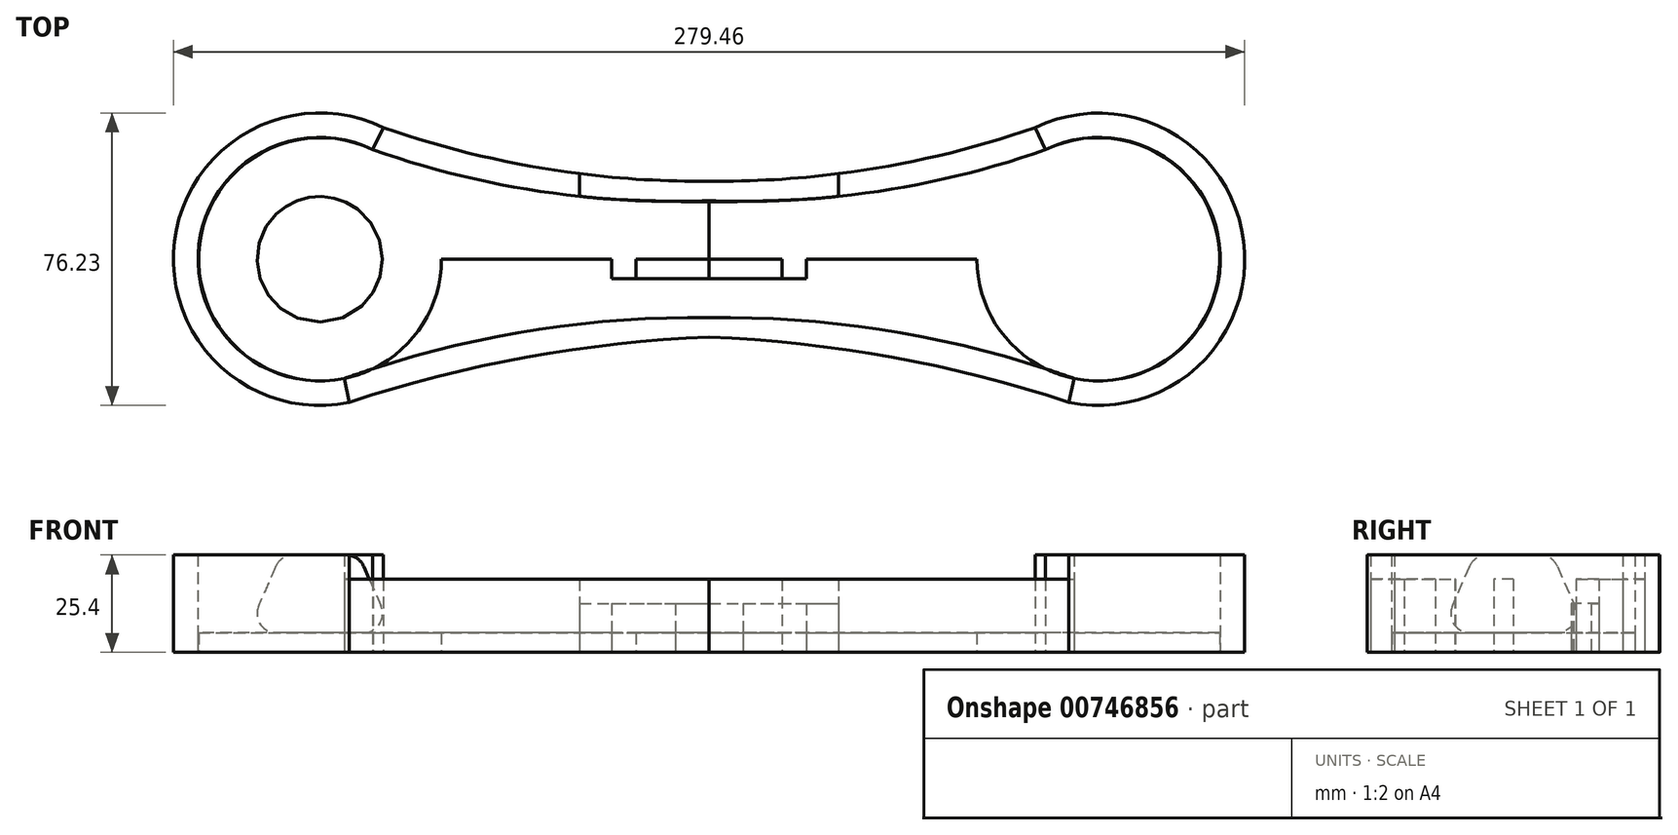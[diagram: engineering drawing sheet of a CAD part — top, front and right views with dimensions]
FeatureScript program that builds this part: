
annotation { "Feature Type Name" : "Feature", "Feature Type Description" : "" }
export const myFeature = defineFeature(function(context is Context, id is Id, definition is map)
    precondition{}
    {
        {
            var Q0;
            Q0=qCreatedBy(makeId("Top.planeOp"),FACE);
            var sketch = newSketch(context, id + "F0", { "sketchPlane" : qUnion([Q0])});
            skLineSegment(sketch, "E0", {"start": v(0, 0) * mm, "end": v(101.6, 0) * mm});
            skCircle(sketch, "E1", {"center": v(101.6, 0) * mm, "radius": 38.1 * mm});
            skCircle(sketch, "E2", {"center": v(101.6, 0) * mm, "radius": 31.75 * mm});
            skLineSegment(sketch, "E3", {"start": v(0, 0) * mm, "end": v(0, 20.32) * mm});
            skLineSegment(sketch, "E4", {"start": v(0, 0) * mm, "end": v(0, -20.32) * mm});
            skPoint(sketch, "E5.endSnap0", {"position": v(93.85, -17.4) * mm});
            skLineSegment(sketch, "E6", {"start": v(93.85, -37.3) * mm, "end": v(95.14, -31.09) * mm});
            skLineSegment(sketch, "E7", {"start": v(85, 34.3) * mm, "end": v(87.76, 28.58) * mm});
            skArc(sketch, "E8", {"start": v(95.14, -31.09) * mm, "mid": v(132.94, 3.88) * mm, "end": v(87.76, 28.58) * mm});
            skArc(sketch, "E9", {"start": v(93.85, -37.3) * mm, "mid": v(139.47, 4.68) * mm, "end": v(85, 34.3) * mm});
            skArc(sketch, "E10", {"start": v(93.85, -37.3) * mm, "mid": v(47.52, -25.54) * mm, "end": v(0, -20.32) * mm});
            skLineSegment(sketch, "E11.MirrorCS", {"start": v(-93.85, -37.3) * mm, "end": v(-95.14, -31.09) * mm});
            skLineSegment(sketch, "E12.MirrorCS", {"start": v(-85, 34.3) * mm, "end": v(-87.76, 28.58) * mm});
            skPoint(sketch, "E13.MirrorP", {"position": v(-93.85, -17.4) * mm});
            skArc(sketch, "E14.MirrorCS", {"start": v(-95.14, -31.09) * mm, "mid": v(-132.94, 3.88) * mm, "end": v(-87.76, 28.58) * mm});
            skCircle(sketch, "E15.MirrorC", {"center": v(-101.6, 0) * mm, "radius": 31.75 * mm});
            skLineSegment(sketch, "E16.MirrorCS", {"start": v(0, 0) * mm, "end": v(-101.6, 0) * mm});
            skArc(sketch, "E17.MirrorCS", {"start": v(-93.85, -37.3) * mm, "mid": v(-47.52, -25.54) * mm, "end": v(0, -20.32) * mm});
            skArc(sketch, "E18.MirrorCS", {"start": v(-93.85, -37.3) * mm, "mid": v(-139.47, 4.68) * mm, "end": v(-85, 34.3) * mm});
            skArc(sketch, "E19", {"start": v(0, 20.32) * mm, "mid": v(43.1, 23.67) * mm, "end": v(85, 34.3) * mm});
            skArc(sketch, "E20.MirrorCS", {"start": v(0, 20.32) * mm, "mid": v(-43.1, 23.67) * mm, "end": v(-85, 34.3) * mm});
            skLineSegment(sketch, "E21", {"start": v(0, 0) * mm, "end": v(-25.4, 0) * mm});
            skLineSegment(sketch, "E22", {"start": v(0, 0) * mm, "end": v(19.05, 0) * mm});
            skLineSegment(sketch, "E23", {"start": v(-25.4, 0) * mm, "end": v(-25.4, -5.08) * mm});
            skLineSegment(sketch, "E24", {"start": v(-25.4, -5.08) * mm, "end": v(19.05, -5.08) * mm});
            skLineSegment(sketch, "E25", {"start": v(19.05, -5.08) * mm, "end": v(19.05, 0) * mm});
            skArc(sketch, "E26", {"start": v(95.14, -31.09) * mm, "mid": v(48.28, -18.9) * mm, "end": v(0, -15.24) * mm});
            skArc(sketch, "E27.MirrorCS", {"start": v(-95.14, -31.09) * mm, "mid": v(-48.28, -18.9) * mm, "end": v(0, -15.24) * mm});
            skArc(sketch, "E28", {"start": v(0, 15.24) * mm, "mid": v(44.51, 17.76) * mm, "end": v(87.76, 28.58) * mm});
            skArc(sketch, "E29.MirrorCS", {"start": v(0, 15.24) * mm, "mid": v(-44.51, 17.76) * mm, "end": v(-87.76, 28.58) * mm});
            skLineSegment(sketch, "E30", {"start": v(19.05, 20.9) * mm, "end": v(-25.4, 21.4) * mm});
            skLineSegment(sketch, "E31", {"start": v(-25.4, 15.65) * mm, "end": v(-25.4, 21.4) * mm});
            skLineSegment(sketch, "E32", {"start": v(0, 0) * mm, "end": v(25.4, 0) * mm});
            skLineSegment(sketch, "E33", {"start": v(25.4, 0) * mm, "end": v(25.4, 21.4) * mm});
            skArc(sketch, "E34", {"start": v(-25.4, 15.65) * mm, "mid": v(0, 15) * mm, "end": v(25.4, 15.65) * mm});
            skLineSegment(sketch, "E35", {"start": v(-33.78, 22.32) * mm, "end": v(-33.78, 16.38) * mm});
            skLineSegment(sketch, "E36", {"start": v(33.78, 22.32) * mm, "end": v(33.78, 16.38) * mm});
            skSolve(sketch);
        }
        {
            var Q0;
            {var subQ1=sQuery(id+"F0.wireOp",EDGE,"E6");Q0=makeQuery(id+"F0.imprint","IMPRINT",FACE,{"disambiguationData":[TD([[makeQuery(id+"F0.imprint","IMPRINT",EDGE,{"derivedFrom":subQ1}),-1.0]])]});}
            var Q1;
            {var subQ0=sQuery(id+"F0.wireOp",EDGE,"E11.MirrorCS");Q1=makeQuery(id+"F0.imprint","IMPRINT",FACE,{"disambiguationData":[TD([[makeQuery(id+"F0.imprint","IMPRINT",EDGE,{"derivedFrom":subQ0}),1.0]])]});}
            extrude(context, id + "F1", {"entities" : qUnion([Q0, Q1]), "depth" : 25.4 * mm, "offsetDistance" : 25.4 * mm});
        }
        {
            var Q0;
            {var subQ0=sQuery(id+"F0.wireOp",EDGE,"E22");Q0=makeQuery(id+"F0.imprint","IMPRINT",FACE,{"disambiguationData":[TD([[makeQuery(id+"F0.imprint","IMPRINT",EDGE,{"derivedFrom":subQ0}),-1.0]])]});}
            var Q1;
            {var subQ0=sQuery(id+"F0.wireOp",EDGE,"E8");Q1=makeQuery(id+"F0.imprint","IMPRINT",FACE,{"disambiguationData":[TD([[makeQuery(id+"F0.imprint","IMPRINT",EDGE,{"derivedFrom":subQ0}),1.0]])]});}
            var Q2;
            {var subQ0=sQuery(id+"F0.wireOp",EDGE,"E14.MirrorCS");Q2=makeQuery(id+"F0.imprint","IMPRINT",FACE,{"disambiguationData":[TD([[makeQuery(id+"F0.imprint","IMPRINT",EDGE,{"derivedFrom":subQ0}),-1.0]])]});}
            var Q3;
            {var subQ0=sQuery(id+"F0.wireOp",EDGE,"E21");Q3=makeQuery(id+"F0.imprint","IMPRINT",FACE,{"disambiguationData":[TD([[makeQuery(id+"F0.imprint","IMPRINT",EDGE,{"derivedFrom":subQ0}),1.0]])]});}
            var Q4;
            {var subQ0=sQuery(id+"F0.wireOp",EDGE,"E25");Q4=makeQuery(id+"F0.imprint","IMPRINT",FACE,{"disambiguationData":[TD([[makeQuery(id+"F0.imprint","IMPRINT",EDGE,{"derivedFrom":subQ0}),-1.0]])]});}
            var Q5;
            {var subQ0=sQuery(id+"F0.wireOp",EDGE,"E23");Q5=makeQuery(id+"F0.imprint","IMPRINT",FACE,{"disambiguationData":[TD([[makeQuery(id+"F0.imprint","IMPRINT",EDGE,{"derivedFrom":subQ0}),-1.0]])]});}
            var Q6;
            {var subQ0=sQuery(id+"F0.wireOp",EDGE,"E21");Q6=makeQuery(id+"F0.imprint","IMPRINT",FACE,{"disambiguationData":[TD([[makeQuery(id+"F0.imprint","IMPRINT",EDGE,{"derivedFrom":subQ0}),-1.0]])]});}
            var Q7;
            {var subQ0=sQuery(id+"F0.wireOp",EDGE,"E22");Q7=makeQuery(id+"F0.imprint","IMPRINT",FACE,{"disambiguationData":[TD([[makeQuery(id+"F0.imprint","IMPRINT",EDGE,{"derivedFrom":subQ0}),1.0]])]});}
            var Q8;
            {var subQ0=sQuery(id+"F0.wireOp",EDGE,"E2");var subQ1=sQuery(id+"F0.wireOp",EDGE,"E0");var subQ2=makeQuery(id+"F0.imprint","INTERSECT",VERTEX,{"derivedFrom":[subQ1,subQ0]});Q8=makeQuery(id+"F0.imprint","IMPRINT",FACE,{"disambiguationData":[TD([[makeQuery(id+"F0.imprint","IMPRINT",EDGE,{"disambiguationData":[TD([[subQ2,1.0]])],"derivedFrom":subQ1}),1.0]])]});}
            var Q9;
            {var subQ0=sQuery(id+"F0.wireOp",EDGE,"E2");var subQ1=sQuery(id+"F0.wireOp",EDGE,"E0");var subQ2=makeQuery(id+"F0.imprint","INTERSECT",VERTEX,{"derivedFrom":[subQ1,subQ0]});Q9=makeQuery(id+"F0.imprint","IMPRINT",FACE,{"disambiguationData":[TD([[makeQuery(id+"F0.imprint","IMPRINT",EDGE,{"disambiguationData":[TD([[subQ2,1.0]])],"derivedFrom":subQ1}),-1.0]])]});}
            var Q10;
            {var subQ1=sQuery(id+"F0.wireOp",EDGE,"E0");var subQ3=sQuery(id+"F0.wireOp",EDGE,"E1");var subQ4=makeQuery(id+"F0.imprint","INTERSECT",VERTEX,{"derivedFrom":[subQ1,subQ3]});Q10=makeQuery(id+"F0.imprint","IMPRINT",FACE,{"disambiguationData":[TD([[makeQuery(id+"F0.imprint","IMPRINT",EDGE,{"disambiguationData":[TD([[subQ4,1.0]])],"derivedFrom":subQ3}),-1.0]])]});}
            var Q11;
            {var subQ4=sQuery(id+"F0.wireOp",EDGE,"E3");var subQ6=sQuery(id+"F0.wireOp",EDGE,"E34");var subQ10=makeQuery(id+"F0.imprint","INTERSECT",VERTEX,{"derivedFrom":[subQ4,subQ6]});Q11=makeQuery(id+"F0.imprint","IMPRINT",FACE,{"disambiguationData":[TD([[makeQuery(id+"F0.imprint","IMPRINT",EDGE,{"disambiguationData":[TD([[subQ10,-1.0]])],"derivedFrom":subQ6}),-1.0]])]});}
            extrude(context, id + "F2", {"entities" : qUnion([Q0, Q1, Q2, Q3, Q4, Q5, Q6, Q7, Q8, Q9, Q10, Q11]), "depth" : 5.08 * mm, "offsetDistance" : 25.4 * mm});
        }
        {
            var Q0;
            Q0=makeQuery(id+"F0.imprint","IMPRINT",FACE,{"disambiguationData":[TD([[makeQuery(id+"F0.imprint","IMPRINT",EDGE,{"derivedFrom":sQuery(id+"F0.wireOp",EDGE,"E12.MirrorCS")}),1.0]])]});
            var Q1;
            {var subQ0=sQuery(id+"F0.wireOp",EDGE,"E10");var subQ1=sQuery(id+"F0.wireOp",EDGE,"E1");var subQ2=makeQuery(id+"F0.imprint","INTERSECT",VERTEX,{"derivedFrom":[subQ1,subQ0]});Q1=makeQuery(id+"F0.imprint","IMPRINT",FACE,{"disambiguationData":[TD([[makeQuery(id+"F0.imprint","IMPRINT",EDGE,{"disambiguationData":[TD([[subQ2,1.0]])],"derivedFrom":subQ1}),-1.0]])]});}
            var Q2;
            {var subQ2=sQuery(id+"F0.wireOp",EDGE,"E11.MirrorCS");Q2=makeQuery(id+"F0.imprint","IMPRINT",FACE,{"disambiguationData":[TD([[makeQuery(id+"F0.imprint","IMPRINT",EDGE,{"derivedFrom":subQ2}),-1.0]])]});}
            var Q3;
            {var subQ1=sQuery(id+"F0.wireOp",EDGE,"E6");Q3=makeQuery(id+"F0.imprint","IMPRINT",FACE,{"disambiguationData":[TD([[makeQuery(id+"F0.imprint","IMPRINT",EDGE,{"derivedFrom":subQ1}),1.0]])]});}
            var Q4;
            {var subQ0=sQuery(id+"F0.wireOp",EDGE,"E7");Q4=makeQuery(id+"F0.imprint","IMPRINT",FACE,{"disambiguationData":[TD([[makeQuery(id+"F0.imprint","IMPRINT",EDGE,{"derivedFrom":subQ0}),-1.0]])]});}
            var Q5;
            {var subQ1=sQuery(id+"F0.wireOp",EDGE,"E1");var subQ3=sQuery(id+"F0.wireOp",EDGE,"E28");var subQ4=makeQuery(id+"F0.imprint","INTERSECT",VERTEX,{"derivedFrom":[subQ1,subQ3]});Q5=makeQuery(id+"F0.imprint","IMPRINT",FACE,{"disambiguationData":[TD([[makeQuery(id+"F0.imprint","IMPRINT",EDGE,{"disambiguationData":[TD([[subQ4,1.0]])],"derivedFrom":subQ3}),1.0]])]});}
            extrude(context, id + "F3", {"entities" : qUnion([Q0, Q1, Q2, Q3, Q4, Q5]), "depth" : 19.05 * mm, "offsetDistance" : 25.4 * mm});
        }
        {
            var Q0;
            {var subQ0=sQuery(id+"F0.wireOp",EDGE,"E19");var subQ1=makeQuery(id+"F0.imprint","INTERSECT",VERTEX,{"derivedFrom":[subQ0,sQuery(id+"F0.wireOp",EDGE,"E30")]});Q0=makeQuery(id+"F0.imprint","IMPRINT",FACE,{"disambiguationData":[TD([[makeQuery(id+"F0.imprint","IMPRINT",EDGE,{"disambiguationData":[TD([[subQ1,-1.0]])],"derivedFrom":subQ0}),-1.0]])]});}
            var Q1;
            {var subQ5=sQuery(id+"F0.wireOp",EDGE,"E31");Q1=makeQuery(id+"F0.imprint","IMPRINT",FACE,{"disambiguationData":[TD([[makeQuery(id+"F0.imprint","IMPRINT",EDGE,{"derivedFrom":subQ5}),-1.0]])]});}
            var Q2;
            {var subQ0=sQuery(id+"F0.wireOp",EDGE,"E31");Q2=makeQuery(id+"F0.imprint","IMPRINT",FACE,{"disambiguationData":[TD([[makeQuery(id+"F0.imprint","IMPRINT",EDGE,{"derivedFrom":subQ0}),1.0]])]});}
            var Q3;
            {var subQ3=sQuery(id+"F0.wireOp",EDGE,"E36");Q3=makeQuery(id+"F0.imprint","IMPRINT",FACE,{"disambiguationData":[TD([[makeQuery(id+"F0.imprint","IMPRINT",EDGE,{"derivedFrom":subQ3}),-1.0]])]});}
            extrude(context, id + "F4", {"entities" : qUnion([Q0, Q1, Q2, Q3]), "depth" : 12.7 * mm, "offsetDistance" : 25.4 * mm});
        }
        {
            var Q0;
            Q0=makeQuery(id+"F2.opExtrude","CAP_FACE",FACE,{"disambiguationData":[OSD([sQuery(id+"F0.wireOp",EDGE,"E4"),sQuery(id+"F0.wireOp",EDGE,"E8"),sQuery(id+"F0.wireOp",EDGE,"E14.MirrorCS"),sQuery(id+"F0.wireOp",EDGE,"E24"),sQuery(id+"F0.wireOp",EDGE,"E25"),sQuery(id+"F0.wireOp",EDGE,"E26"),sQuery(id+"F0.wireOp",EDGE,"E27.MirrorCS"),sQuery(id+"F0.wireOp",EDGE,"E28"),sQuery(id+"F0.wireOp",EDGE,"E29.MirrorCS"),sQuery(id+"F0.wireOp",EDGE,"E32"),sQuery(id+"F0.wireOp",EDGE,"E34")])],"isStart":false});
            var sketch = newSketch(context, id + "F5", { "sketchPlane" : qUnion([Q0])});
            skArc(sketch, "E37.0", {"start": v(-95.14, -31.09) * mm, "mid": v(-133.1, 3.9) * mm, "end": v(-87.76, 28.58) * mm});
            skCircle(sketch, "E38", {"center": v(-101.6, 0) * mm, "radius": 19.05 * mm});
            skSolve(sketch);
        }
        {
            var Q0;
            Q0=qCreatedBy(makeId("Top.planeOp"),FACE);
            cPlane(context, id + "F6", {"entities" : qUnion([Q0]), "cplaneType" : CPlaneType.OFFSET, "offset" : 25.4 * mm, "width" : 152.4 * mm, "height" : 152.4 * mm});
        }
        {
            var Q0;
            Q0=qCreatedBy(id+"F6.planeOp",FACE);
            var sketch = newSketch(context, id + "F7", { "sketchPlane" : qUnion([Q0])});
            skPoint(sketch, "E39.0", {"position": v(-101.6, 0) * mm});
            skCircle(sketch, "E40", {"center": v(-101.6, 0) * mm, "radius": 10.16 * mm});
            skSolve(sketch);
        }
        {
            var Q1;
            Q1=makeQuery(id+"F5.imprint","IMPRINT",FACE,{"disambiguationData":[TD([[makeQuery(id+"F5.imprint","IMPRINT",EDGE,{"derivedFrom":sQuery(id+"F5.wireOp",EDGE,"E38")}),1.0]])]});
            var Q2;
            Q2=makeQuery(id+"F7.imprint","IMPRINT",FACE,{"disambiguationData":[TD([[makeQuery(id+"F7.imprint","IMPRINT",EDGE,{"derivedFrom":sQuery(id+"F7.wireOp",EDGE,"E40")}),1.0]])]});
            loft(context, id + "F8", {"operationType" : NewBodyOperationType.ADD, "sheetProfilesArray" : [{ "sheetProfileEntities" : qUnion([Q1]) }, { "sheetProfileEntities" : qUnion([Q2]) }]});
        }
        {
            var Q0;
            Q0=makeQuery(id+"F8.opLoft","MID_CAP_EDGE",EDGE,{"disambiguationData":[OSD([sQuery(id+"F7.wireOp",EDGE,"E40")])],"capPos":1.0});
            var Q1;
            Q1=makeQuery(id+"F8.opLoft","MID_CAP_EDGE",EDGE,{"disambiguationData":[OSD([sQuery(id+"F5.wireOp",EDGE,"E38")])],"capPos":0.0});
            fillet(context, id + "F9", {"entities" : qUnion([Q0, Q1]), "radius" : 5.08 * mm, "tangentPropagation" : true, "allowEdgeOverflow" : false});
        }
        {
            var Q0;
            Q0=makeQuery(id+"F2.opExtrude","SWEPT_BODY",BODY,{"disambiguationData":[OSD([sQuery(id+"F0.wireOp",EDGE,"E4"),sQuery(id+"F0.wireOp",EDGE,"E8"),sQuery(id+"F0.wireOp",EDGE,"E14.MirrorCS"),sQuery(id+"F0.wireOp",EDGE,"E24"),sQuery(id+"F0.wireOp",EDGE,"E25"),sQuery(id+"F0.wireOp",EDGE,"E26"),sQuery(id+"F0.wireOp",EDGE,"E27.MirrorCS"),sQuery(id+"F0.wireOp",EDGE,"E28"),sQuery(id+"F0.wireOp",EDGE,"E29.MirrorCS"),sQuery(id+"F0.wireOp",EDGE,"E32"),sQuery(id+"F0.wireOp",EDGE,"E34")])]});
            var Q1;
            Q1=qCreatedBy(makeId("Right.planeOp"),FACE);
            mirror(context, id + "F10", {"entities" : qUnion([Q0]), "mirrorPlane" : qUnion([Q1])});
        }
        {
            var Q0;
            {var subQ5=sQuery(id+"F0.wireOp",EDGE,"E25");Q0=makeQuery(id+"F0.imprint","IMPRINT",FACE,{"disambiguationData":[TD([[makeQuery(id+"F0.imprint","IMPRINT",EDGE,{"derivedFrom":subQ5}),1.0]])]});}
            var Q1;
            {var subQ0=sQuery(id+"F0.wireOp",EDGE,"E21");Q1=makeQuery(id+"F0.imprint","IMPRINT",FACE,{"disambiguationData":[TD([[makeQuery(id+"F0.imprint","IMPRINT",EDGE,{"derivedFrom":subQ0}),1.0]])]});}
            extrude(context, id + "F11", {"entities" : qUnion([Q0, Q1]), "depth" : 19.05 * mm, "offsetDistance" : 25.4 * mm});
        }
    });
